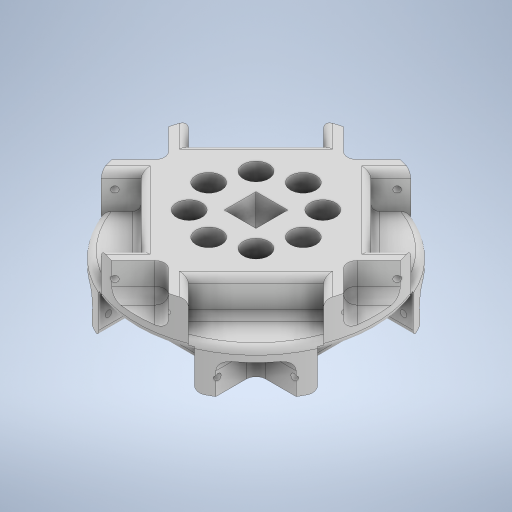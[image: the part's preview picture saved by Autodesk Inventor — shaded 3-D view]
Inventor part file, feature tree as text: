
AUTODESK INVENTOR PART (.ipt)
format: ipt  version: 2024.2 (Build 282272000, 272)  size: 687,104 bytes
history: native  units: mm
features: extrude x9, sketch x9, fillet x5, pattern_circular x5
ambient origin geometry x8: Origin, YZ Plane, XZ Plane, XY Plane, X Axis, Y Axis, Z Axis, Center Point
bodies: Solid1 (feature_tree)
feature tree (28):
  extrude  "Extrusion1"  Depth=25.0mm TaperAngle=0.0deg
  extrude  "Extrusion2"  TaperAngle=45.0deg  [1 undecoded]
  extrude  "Extrusion3"  Depth=11.0mm TaperAngle=0.0deg
  extrude  "Extrusion4"  Depth=12.0mm
  fillet  "Fillet1"  Radius=11.0mm
  pattern_circular  "Circular Pattern2"  Count=4 Angle=360.0deg
  extrude  "Extrusion5"  Depth=2.0mm
  fillet  "Fillet2"  Radius=2.0mm
  pattern_circular  "Circular Pattern3"  [2 undecoded]
  extrude  "Extrusion6"  Depth=2.0mm
  extrude  "Extrusion7"  Depth=2.0mm TaperAngle=360.0deg
  fillet  "Fillet3"  Radius=10.0mm
  pattern_circular  "Circular Pattern4"  [2 undecoded]
  extrude  "Extrusion8"  TaperAngle=0.0deg  [1 undecoded]
  fillet  "Fillet4"  Radius=3.0mm
  pattern_circular  "Circular Pattern5"  Angle=90.0deg  [1 undecoded]
  extrude  "Extrusion9"  TaperAngle=45.0deg  [1 undecoded]
  pattern_circular  "Circular Pattern6"  Count=2  [1 undecoded]
  fillet  "Fillet5"  Radius=10.0mm
  sketch  "Sketch1"  dims[d0=75.0mm d1=25.0mm d2=0.0mm]
  sketch  "Sketch2"  dims[d3=30.0mm d5=45.0deg]
  sketch  "Sketch3"  dims[d6=12.0mm d7=11.0mm d8=0.0mm]
  sketch  "Sketch4"  dims[d12=30.0mm d14=12.0mm d15=11.0mm d16=0.0mm]
  sketch  "Sketch5"  dims[d17=5.0mm]
  sketch  "Sketch6"  dims[d18=3.0mm]
  sketch  "Sketch7"  dims[d19=2.0mm]
  sketch  "Sketch8"  dims[d20=0.0mm d21=0.0mm]
  sketch  "Sketch9"  dims[d22=2.0mm d23=40.0mm d24=360.0deg d26=5.0mm d28=2.0mm d29=0.0mm d30=0.0mm d31=2.0mm d32=40.0mm d33=360.0deg d35=10.0mm d36=10.0mm d37=0.0mm d38=0.0mm d39=3.0mm d40=90.0deg d41=45.0deg d42=20.0mm d43=10.0mm d44=0.0mm d45=3.0mm d46=40.0mm d47=360.0deg d49=20.0mm d50=20.0mm d51=10.0mm d52=0.0mm d53=3.0mm d54=40.0mm d55=360.0deg d57=8.0mm d58=13.0mm d59=13.0mm d60=0.0mm d61=0.0mm d62=80.0mm d63=360.0deg d65=2.0mm]
note: 9 required parameter values undecoded (feature->parameter linkage not recoverable at this tier; creation-order binding heuristic only, values carry confidence <= 0.55)
